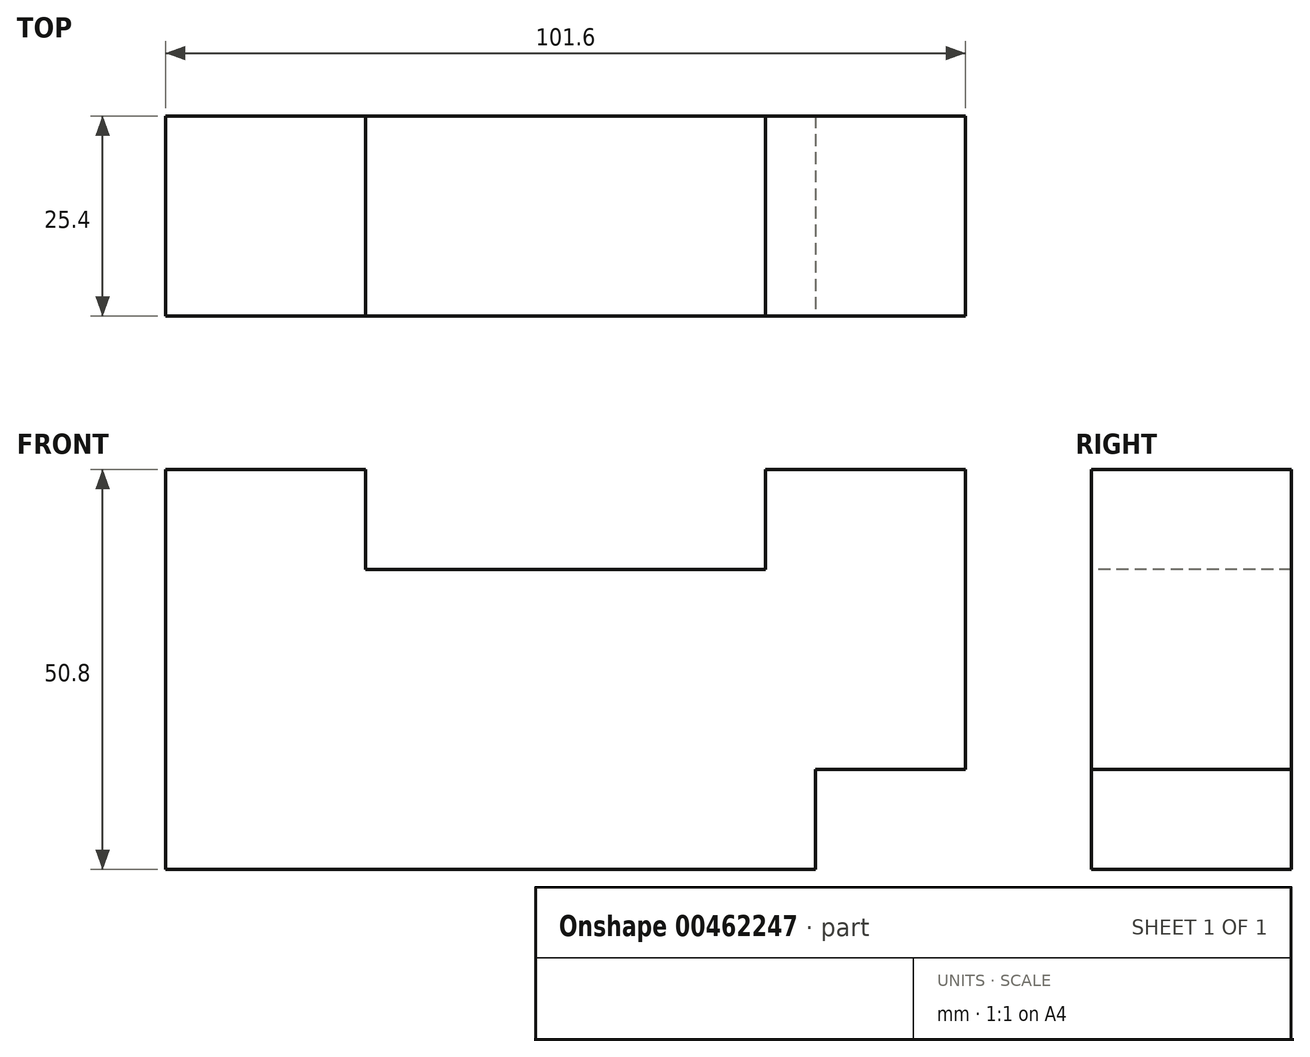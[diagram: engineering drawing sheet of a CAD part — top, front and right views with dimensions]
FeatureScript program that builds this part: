
annotation { "Feature Type Name" : "Feature", "Feature Type Description" : "" }
export const myFeature = defineFeature(function(context is Context, id is Id, definition is map)
    precondition{}
    {
        {
            var Q0;
            Q0=qCreatedBy(makeId("Front.planeOp"),FACE);
            var sketch = newSketch(context, id + "F0", { "sketchPlane" : qUnion([Q0])});
            skLineSegment(sketch, "E0.bottom", {"start": v(-50.8, 25.4) * mm, "end": v(50.8, 25.4) * mm});
            skLineSegment(sketch, "E0.top", {"start": v(-50.8, -25.4) * mm, "end": v(50.8, -25.4) * mm});
            skLineSegment(sketch, "E0.left", {"start": v(-50.8, 25.4) * mm, "end": v(-50.8, -25.4) * mm});
            skLineSegment(sketch, "E0.right", {"start": v(50.8, 25.4) * mm, "end": v(50.8, -25.4) * mm});
            skPoint(sketch, "E0.middle", {"position": v(0, 0) * mm});
            skSolve(sketch);
        }
        {
            var Q0;
            Q0=makeQuery(id+"F0.imprint","IMPRINT",FACE,{"disambiguationData":[TD([[makeQuery(id+"F0.imprint","IMPRINT",EDGE,{"derivedFrom":sQuery(id+"F0.wireOp",EDGE,"E0.bottom")}),-1.0]])]});
            extrude(context, id + "F1", {"entities" : qUnion([Q0]), "endBound" : BoundingType.SYMMETRIC, "depth" : 25.4 * mm});
        }
        {
            var Q0;
            Q0=makeQuery(id+"F1.opExtrude","CAP_FACE",FACE,{"disambiguationData":[OSD([sQuery(id+"F0.wireOp",EDGE,"E0.bottom"),sQuery(id+"F0.wireOp",EDGE,"E0.top"),sQuery(id+"F0.wireOp",EDGE,"E0.left"),sQuery(id+"F0.wireOp",EDGE,"E0.right")])],"isStart":false});
            var sketch = newSketch(context, id + "F2", { "sketchPlane" : qUnion([Q0])});
            skLineSegment(sketch, "E1.bottom", {"start": v(50.8, -25.4) * mm, "end": v(31.75, -25.4) * mm});
            skLineSegment(sketch, "E1.top", {"start": v(50.8, -12.7) * mm, "end": v(31.75, -12.7) * mm});
            skLineSegment(sketch, "E1.left", {"start": v(50.8, -25.4) * mm, "end": v(50.8, -12.7) * mm});
            skLineSegment(sketch, "E1.right", {"start": v(31.75, -25.4) * mm, "end": v(31.75, -12.7) * mm});
            skSolve(sketch);
        }
        {
            var Q0;
            Q0=makeQuery(id+"F2.imprint","IMPRINT",FACE,{"disambiguationData":[TD([[makeQuery(id+"F2.imprint","IMPRINT",EDGE,{"derivedFrom":sQuery(id+"F2.wireOp",EDGE,"E1.bottom")}),1.0]])]});
            extrude(context, id + "F3", {"entities" : qUnion([Q0]), "operationType" : NewBodyOperationType.REMOVE, "endBound" : BoundingType.THROUGH_ALL, "oppositeDirection" : true, "depth" : 25.4 * mm});
        }
        {
            var Q0;
            Q0=makeQuery(id+"F1.opExtrude","CAP_FACE",FACE,{"disambiguationData":[OSD([sQuery(id+"F0.wireOp",EDGE,"E0.bottom"),sQuery(id+"F0.wireOp",EDGE,"E0.top"),sQuery(id+"F0.wireOp",EDGE,"E0.left"),sQuery(id+"F0.wireOp",EDGE,"E0.right")])],"isStart":false});
            var sketch = newSketch(context, id + "F4", { "sketchPlane" : qUnion([Q0])});
            skLineSegment(sketch, "E2.bottom", {"start": v(-25.4, 25.4) * mm, "end": v(25.4, 25.4) * mm});
            skLineSegment(sketch, "E2.top", {"start": v(-25.4, 12.7) * mm, "end": v(25.4, 12.7) * mm});
            skLineSegment(sketch, "E2.left", {"start": v(-25.4, 25.4) * mm, "end": v(-25.4, 12.7) * mm});
            skLineSegment(sketch, "E2.right", {"start": v(25.4, 25.4) * mm, "end": v(25.4, 12.7) * mm});
            skPoint(sketch, "E2.middle", {"position": v(0, 19.05) * mm});
            skSolve(sketch);
        }
        {
            var Q0;
            Q0=makeQuery(id+"F4.imprint","IMPRINT",FACE,{"disambiguationData":[TD([[makeQuery(id+"F4.imprint","IMPRINT",EDGE,{"derivedFrom":sQuery(id+"F4.wireOp",EDGE,"E2.bottom")}),-1.0]])]});
            extrude(context, id + "F5", {"entities" : qUnion([Q0]), "operationType" : NewBodyOperationType.REMOVE, "endBound" : BoundingType.THROUGH_ALL, "oppositeDirection" : true, "depth" : 25.4 * mm});
        }
    });
